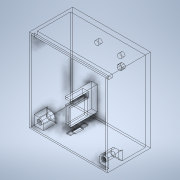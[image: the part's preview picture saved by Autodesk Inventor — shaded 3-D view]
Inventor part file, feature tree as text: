
AUTODESK INVENTOR PART (.ipt)
format: ipt  version: 2021 (Build 250183000, 183)  size: 416,768 bytes
history: native  units: mm
features: extrude x19, sketch x10, plane x4, other x1, fillet x1
ambient origin geometry x8: Origin, YZ Plane, XZ Plane, XY Plane, X Axis, Y Axis, Z Axis, Center Point
bodies: Body1 (feature_tree)
feature tree (35):
  other  "Sólido1"
  sketch  "Boceto1"  dims[d0=0.0mm d1=37.5mm]
  extrude  "Extrusión1"  Depth=37.5mm
  sketch  "Boceto2"  dims[d3=1.5mm d4=2.0mm]
  extrude  "Extrusión2"  Depth=2.0mm
  extrude  "Extrusión4"  Depth=3.5mm
  extrude  "Extrusión3"  TaperAngle=0.0deg  [1 undecoded]
  extrude  "Extrusión5"  Depth=10.0mm
  extrude  "Extrusión6"  Depth=15.0mm
  plane  "Plano de trabajo1"
  extrude  "Extrusión7"  TaperAngle=45.0deg  [1 undecoded]
  plane  "Plano de trabajo2"
  extrude  "Extrusión8"  Depth=2.5mm
  plane  "Plano de trabajo3"
  sketch  "Boceto6"  dims[d11=0.0mm d12=15.0mm]
  extrude  "Extrusión12"  TaperAngle=30.0deg  [1 undecoded]
  sketch  "Boceto9"  dims[d15=2.5mm d16=62.797435mm]
  extrude  "Extrusión13"  Depth=2.0mm
  extrude  "Extrusión14"  TaperAngle=150.0deg  [1 undecoded]
  sketch  "Boceto11"  dims[d17=15.0mm d18=30.0deg]
  extrude  "Extrusión15"  Depth=2.0mm
  extrude  "Extrusión16"  Depth=2.0mm
  plane  "Plano de trabajo4"
  sketch  "Boceto12"  dims[d19=19.333333mm d20=19.333333mm d21=150.0deg d22=2.0mm d24=2.0mm d25=40.0mm d26=0.0mm d27=1.5mm d28=0.0mm d29=12.0mm d30=0.0mm d31=2.0mm d32=80.0mm d33=0.0mm d40=39.5mm d41=0.0mm d46=0.0mm d48=2.0mm d49=37.5mm d50=37.5mm d51=1.5mm d52=80.0mm d53=0.0mm d55=3.0mm d56=0.0mm d57=-80.0mm d74=35.0mm d75=72.0mm d76=36.0mm d77=5.0mm d79=5.0mm d80=5.0mm d81=5.0mm d82=8.0mm d83=8.0mm d84=3.5mm d85=0.0mm d88=4.0mm d89=4.0mm d90=11.0mm d91=4.0mm d92=11.0mm d93=4.0mm d94=65.0mm d95=8.0mm d96=8.0mm d97=15.0mm d98=2.0mm d99=0.0mm d100=1.5mm d102=4.0mm d103=4.0mm d104=1.0mm d105=10.0mm d106=0.0mm d107=2.0mm d108=13.0mm d110=22.5mm d111=36.0mm d112=52.0mm d113=25.0mm d114=14.0mm d115=27.0mm d116=5.4mm d117=2.5mm d118=2.5mm d119=2.5mm d120=2.5mm d121=3.0mm d122=3.0mm d123=2.5mm d124=2.5mm d125=2.5mm d126=2.5mm d127=3.0mm d128=3.0mm d129=0.0mm d130=0.0mm d131=1.5mm d132=0.0mm d134=7.5mm d135=1.5mm d136=1.5mm d137=1.5mm d138=1.5mm d139=72.0mm d140=77.0mm d141=35.0mm d144=3.0mm d145=72.0mm d146=77.0mm d147=5.0mm d148=5.0mm d149=72.0mm d150=5.0mm d151=5.0mm d152=8.0mm d153=8.0mm d154=4.5mm d155=4.5mm d156=11.0mm d157=0.0mm d158=9.0mm d159=0.0mm d160=1.5mm d161=3.5mm d162=14.0mm d163=8.5mm d164=17.2mm d165=3.6mm d166=8.5mm d167=4.0mm d168=3.2mm d169=8.0mm d171=1.5mm d172=1.5mm d173=0.0mm d174=0.7mm d175=0.0mm d176=2.4mm d177=1.5mm d178=22.5mm d179=0.0mm d180=6.5mm d181=0.0mm d182=29.5mm d183=0.0mm d184=27.8mm d185=0.0mm d186=2.0mm]
  extrude  "Extrusión21"  Depth=40.0mm
  extrude  "Extrusión17"  TaperAngle=0.0deg  [1 undecoded]
  extrude  "Extrusión18"  Depth=1.5mm
  extrude  "Extrusión22"  TaperAngle=0.0deg  [1 undecoded]
  extrude  "Extrusión19"  Depth=12.0mm
  extrude  "Extrusión20"  TaperAngle=0.0deg  [1 undecoded]
  fillet  "Empalme1"  Radius=2.0mm
  sketch  "Boceto3"  dims[d5=1.5mm d6=3.5mm]
  sketch  "Boceto4"  dims[d7=2.0mm d8=0.0mm]
  sketch  "Boceto5"  dims[d9=10.0mm d10=116.0mm]
  sketch  "Boceto8"  dims[d13=60.0deg d14=45.0deg]
note: 7 required parameter values undecoded (feature->parameter linkage not recoverable at this tier; creation-order binding heuristic only, values carry confidence <= 0.55)
